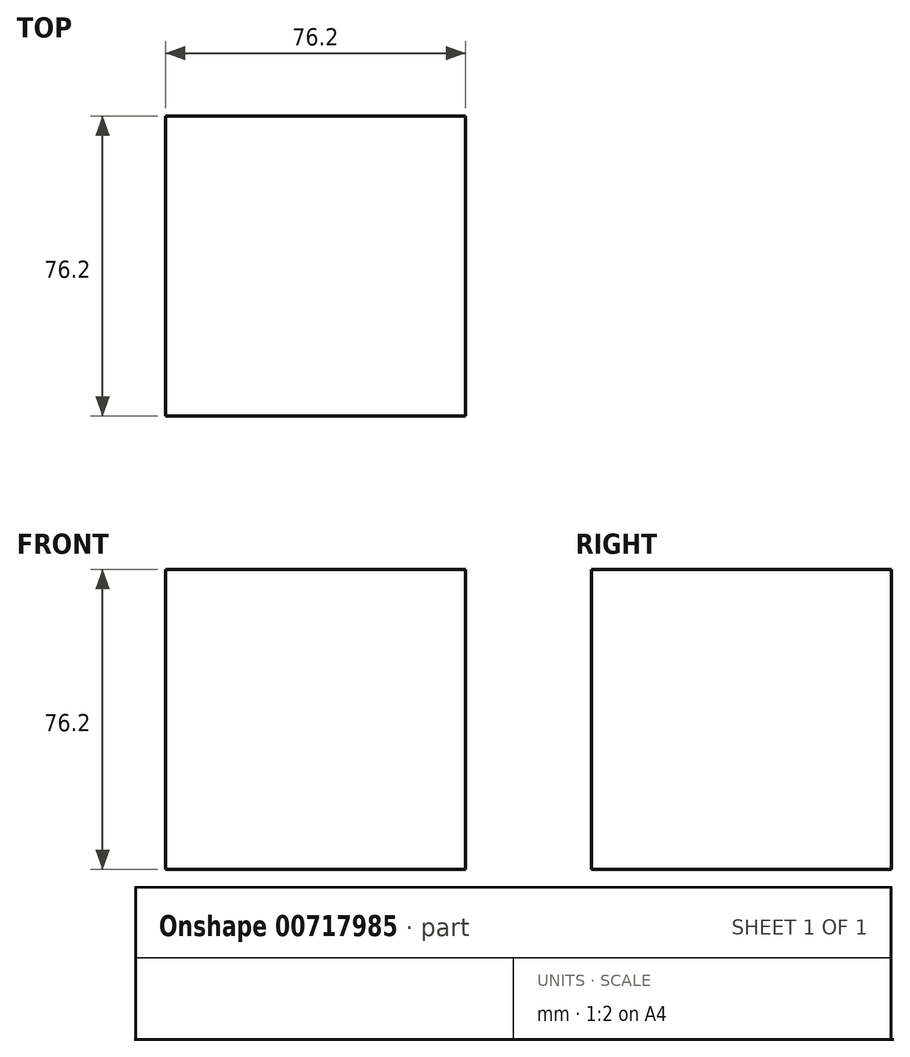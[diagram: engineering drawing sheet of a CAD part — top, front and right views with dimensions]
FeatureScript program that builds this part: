
annotation { "Feature Type Name" : "Feature", "Feature Type Description" : "" }
export const myFeature = defineFeature(function(context is Context, id is Id, definition is map)
    precondition{}
    {
        {
            var Q0;
            Q0=qCreatedBy(makeId("Front.planeOp"),FACE);
            var sketch = newSketch(context, id + "F0", { "sketchPlane" : qUnion([Q0])});
            skLineSegment(sketch, "E0.bottom", {"start": v(-54.08, 27) * mm, "end": v(22.12, 27) * mm});
            skLineSegment(sketch, "E0.top", {"start": v(-54.08, -49.2) * mm, "end": v(22.12, -49.2) * mm});
            skLineSegment(sketch, "E0.left", {"start": v(-54.08, 27) * mm, "end": v(-54.08, -49.2) * mm});
            skLineSegment(sketch, "E0.right", {"start": v(22.12, 27) * mm, "end": v(22.12, -49.2) * mm});
            skSolve(sketch);
        }
        {
            var Q0;
            Q0=makeQuery(id+"F0.imprint","IMPRINT",FACE,{"disambiguationData":[TD([[makeQuery(id+"F0.imprint","IMPRINT",EDGE,{"derivedFrom":sQuery(id+"F0.wireOp",EDGE,"E0.bottom")}),-1.0]])]});
            extrude(context, id + "F1", {"entities" : qUnion([Q0]), "depth" : 76.2 * mm, "offsetDistance" : 25.4 * mm});
        }
    });
